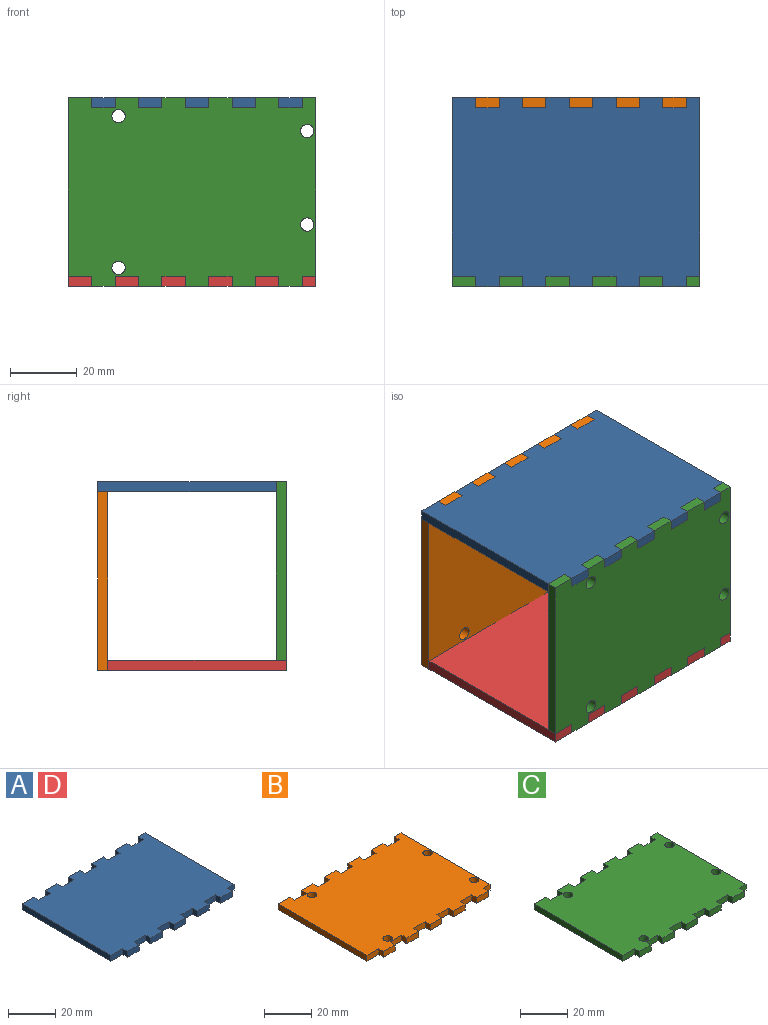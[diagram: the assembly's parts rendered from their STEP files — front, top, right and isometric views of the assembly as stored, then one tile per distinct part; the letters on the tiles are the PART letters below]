
ASSEMBLY  parts=4 mates=3
PART A: 46 faces, bbox 74x56.5x3 mm
  f0: plane 53.5x3mm, normal (-1,0,0), area 160.5mm2, adj f1,f43,f44,f45
  f1: plane 7x3mm, normal (0,-1,0), area 21mm2, adj f0,f2,f44,f45
  f2: plane 3x3mm, normal (-1,0,0), area 9mm2, adj f1,f3,f44,f45
  f3: plane 7x3mm, normal (0,-1,0), area 21mm2, adj f2,f4,f44,f45
  f4: plane 3x3mm, normal (1,0,0), area 9mm2, adj f3,f5,f44,f45
  f5: plane 7x3mm, normal (0,-1,0), area 21mm2, adj f4,f6,f44,f45
  f6: plane 3x3mm, normal (-1,0,0), area 9mm2, adj f5,f7,f44,f45
  f7: plane 7x3mm, normal (0,-1,0), area 21mm2, adj f6,f8,f44,f45
  f8: plane 3x3mm, normal (1,0,0), area 9mm2, adj f7,f9,f44,f45
  f9: plane 7x3mm, normal (0,-1,0), area 21mm2, adj f8,f10,f44,f45
  f10: plane 3x3mm, normal (-1,0,0), area 9mm2, adj f9,f11,f44,f45
  f11: plane 7x3mm, normal (0,-1,0), area 21mm2, adj f10,f12,f44,f45
  f12: plane 3x3mm, normal (1,0,0), area 9mm2, adj f11,f13,f44,f45
  f13: plane 7x3mm, normal (0,-1,0), area 21mm2, adj f12,f14,f44,f45
  f14: plane 3x3mm, normal (-1,0,0), area 9mm2, adj f13,f15,f44,f45
  f15: plane 7x3mm, normal (0,-1,0), area 21mm2, adj f14,f16,f44,f45
  f16: plane 3x3mm, normal (1,0,0), area 9mm2, adj f15,f17,f44,f45
  f17: plane 7x3mm, normal (0,-1,0), area 21mm2, adj f16,f18,f44,f45
  f18: plane 3x3mm, normal (-1,0,0), area 9mm2, adj f17,f19,f44,f45
  f19: plane 7x3mm, normal (0,-1,0), area 21mm2, adj f18,f20,f44,f45
  f20: plane 3x3mm, normal (1,0,0), area 9mm2, adj f19,f21,f44,f45
  f21: plane 4x3mm, normal (0,-1,0), area 12mm2, adj f20,f22,f44,f45
  f22: plane 53.5x3mm, normal (1,0,0), area 160.5mm2, adj f21,f23,f44,f45
  f23: plane 4x3mm, normal (0,1,0), area 12mm2, adj f22,f24,f44,f45
  f24: plane 3x3mm, normal (-1,0,0), area 9mm2, adj f23,f25,f44,f45
  f25: plane 7x3mm, normal (0,1,0), area 21mm2, adj f24,f26,f44,f45
  f26: plane 3x3mm, normal (1,0,0), area 9mm2, adj f25,f27,f44,f45
  f27: plane 7x3mm, normal (0,1,0), area 21mm2, adj f26,f28,f44,f45
  f28: plane 3x3mm, normal (-1,0,0), area 9mm2, adj f27,f29,f44,f45
  f29: plane 7x3mm, normal (0,1,0), area 21mm2, adj f28,f30,f44,f45
  f30: plane 3x3mm, normal (1,0,0), area 9mm2, adj f29,f31,f44,f45
  f31: plane 7x3mm, normal (0,1,0), area 21mm2, adj f30,f32,f44,f45
  f32: plane 3x3mm, normal (-1,0,0), area 9mm2, adj f31,f33,f44,f45
  f33: plane 7x3mm, normal (0,1,0), area 21mm2, adj f32,f34,f44,f45
  f34: plane 3x3mm, normal (1,0,0), area 9mm2, adj f33,f35,f44,f45
  f35: plane 7x3mm, normal (0,1,0), area 21mm2, adj f34,f36,f44,f45
  f36: plane 3x3mm, normal (-1,0,0), area 9mm2, adj f35,f37,f44,f45
  f37: plane 7x3mm, normal (0,1,0), area 21mm2, adj f36,f38,f44,f45
  f38: plane 3x3mm, normal (1,0,0), area 9mm2, adj f37,f39,f44,f45
  f39: plane 7x3mm, normal (0,1,0), area 21mm2, adj f38,f40,f44,f45
  f40: plane 3x3mm, normal (-1,0,0), area 9mm2, adj f39,f41,f44,f45
  f41: plane 7x3mm, normal (0,1,0), area 21mm2, adj f40,f42,f44,f45
  f42: plane 3x3mm, normal (1,0,0), area 9mm2, adj f41,f43,f44,f45
  f43: plane 7x3mm, normal (0,1,0), area 21mm2, adj f0,f42,f44,f45
  f44: plane 74x56.5mm, normal (0,0,1), area 3959mm2, adj f0,f1,f2,f3,f4,f5,f6,f7
  f45: plane 74x56.5mm, normal (0,0,-1), area 3959mm2, adj f0,f1,f2,f3,f4,f5,f6,f7
PART B: 50 faces, bbox 74x56.5x3 mm
  f0: plane 74x56.5mm, normal (0,0,1), area 3908.7mm2, adj f2,f3,f4,f5,f6,f7,f8,f9
  f1: plane 74x56.5mm, normal (0,0,-1), area 3908.7mm2, adj f2,f3,f4,f5,f6,f7,f8,f9
  f2: plane 53.5x3mm, normal (-1,0,0), area 160.5mm2, adj f0,f1,f3,f45
  f3: plane 7x3mm, normal (0,-1,0), area 21mm2, adj f0,f1,f2,f4
  f4: plane 3x3mm, normal (-1,0,0), area 9mm2, adj f0,f1,f3,f5
  f5: plane 7x3mm, normal (0,-1,0), area 21mm2, adj f0,f1,f4,f6
  f6: plane 3x3mm, normal (1,0,0), area 9mm2, adj f0,f1,f5,f7
  f7: plane 7x3mm, normal (0,-1,0), area 21mm2, adj f0,f1,f6,f8
  f8: plane 3x3mm, normal (-1,0,0), area 9mm2, adj f0,f1,f7,f9
  f9: plane 7x3mm, normal (0,-1,0), area 21mm2, adj f0,f1,f8,f10
  f10: plane 3x3mm, normal (1,0,0), area 9mm2, adj f0,f1,f9,f11
  f11: plane 7x3mm, normal (0,-1,0), area 21mm2, adj f0,f1,f10,f12
  f12: plane 3x3mm, normal (-1,0,0), area 9mm2, adj f0,f1,f11,f13
  f13: plane 7x3mm, normal (0,-1,0), area 21mm2, adj f0,f1,f12,f14
  f14: plane 3x3mm, normal (1,0,0), area 9mm2, adj f0,f1,f13,f15
  f15: plane 7x3mm, normal (0,-1,0), area 21mm2, adj f0,f1,f14,f16
  f16: plane 3x3mm, normal (-1,0,0), area 9mm2, adj f0,f1,f15,f17
  f17: plane 7x3mm, normal (0,-1,0), area 21mm2, adj f0,f1,f16,f18
  f18: plane 3x3mm, normal (1,0,0), area 9mm2, adj f0,f1,f17,f19
  f19: plane 7x3mm, normal (0,-1,0), area 21mm2, adj f0,f1,f18,f20
  f20: plane 3x3mm, normal (-1,0,0), area 9mm2, adj f0,f1,f19,f21
  f21: plane 7x3mm, normal (0,-1,0), area 21mm2, adj f0,f1,f20,f22
  f22: plane 3x3mm, normal (1,0,0), area 9mm2, adj f0,f1,f21,f23
  f23: plane 4x3mm, normal (0,-1,0), area 12mm2, adj f0,f1,f22,f24
  f24: plane 53.5x3mm, normal (1,0,0), area 160.5mm2, adj f0,f1,f23,f25
  f25: plane 4x3mm, normal (0,1,0), area 12mm2, adj f0,f1,f24,f26
  f26: plane 3x3mm, normal (-1,0,0), area 9mm2, adj f0,f1,f25,f27
  f27: plane 7x3mm, normal (0,1,0), area 21mm2, adj f0,f1,f26,f28
  f28: plane 3x3mm, normal (1,0,0), area 9mm2, adj f0,f1,f27,f29
  f29: plane 7x3mm, normal (0,1,0), area 21mm2, adj f0,f1,f28,f30
  f30: plane 3x3mm, normal (-1,0,0), area 9mm2, adj f0,f1,f29,f31
  f31: plane 7x3mm, normal (0,1,0), area 21mm2, adj f0,f1,f30,f32
  f32: plane 3x3mm, normal (1,0,0), area 9mm2, adj f0,f1,f31,f33
  f33: plane 7x3mm, normal (0,1,0), area 21mm2, adj f0,f1,f32,f34
  f34: plane 3x3mm, normal (-1,0,0), area 9mm2, adj f0,f1,f33,f35
  f35: plane 7x3mm, normal (0,1,0), area 21mm2, adj f0,f1,f34,f36
  f36: plane 3x3mm, normal (1,0,0), area 9mm2, adj f0,f1,f35,f37
  f37: plane 7x3mm, normal (0,1,0), area 21mm2, adj f0,f1,f36,f38
  f38: plane 3x3mm, normal (-1,0,0), area 9mm2, adj f0,f1,f37,f39
  f39: plane 7x3mm, normal (0,1,0), area 21mm2, adj f0,f1,f38,f40
  f40: plane 3x3mm, normal (1,0,0), area 9mm2, adj f0,f1,f39,f41
  f41: plane 7x3mm, normal (0,1,0), area 21mm2, adj f0,f1,f40,f42
  f42: plane 3x3mm, normal (-1,0,0), area 9mm2, adj f0,f1,f41,f43
  f43: plane 7x3mm, normal (0,1,0), area 21mm2, adj f0,f1,f42,f44
  f44: plane 3x3mm, normal (1,0,0), area 9mm2, adj f0,f1,f43,f45
  f45: plane 7x3mm, normal (0,1,0), area 21mm2, adj f0,f1,f2,f44
  f46: cylinder r=2mm len=4mm, axis (0,0,1), area 37.7mm2, adj f0,f1
  f47: cylinder r=2mm len=4mm, axis (0,0,1), area 37.7mm2, adj f0,f1
  f48: cylinder r=2mm len=4mm, axis (0,0,1), area 37.7mm2, adj f0,f1
  f49: cylinder r=2mm len=4mm, axis (0,0,1), area 37.7mm2, adj f0,f1
PART C: 50 faces, bbox 74x56.5x3 mm
  f0: plane 74x56.5mm, normal (0,0,1), area 3908.7mm2, adj f2,f3,f4,f5,f6,f7,f8,f9
  f1: plane 74x56.5mm, normal (0,0,-1), area 3908.7mm2, adj f2,f3,f4,f5,f6,f7,f8,f9
  f2: plane 53.5x3mm, normal (-1,0,0), area 160.5mm2, adj f0,f1,f3,f45
  f3: plane 7x3mm, normal (0,-1,0), area 21mm2, adj f0,f1,f2,f4
  f4: plane 3x3mm, normal (-1,0,0), area 9mm2, adj f0,f1,f3,f5
  f5: plane 7x3mm, normal (0,-1,0), area 21mm2, adj f0,f1,f4,f6
  f6: plane 3x3mm, normal (1,0,0), area 9mm2, adj f0,f1,f5,f7
  f7: plane 7x3mm, normal (0,-1,0), area 21mm2, adj f0,f1,f6,f8
  f8: plane 3x3mm, normal (-1,0,0), area 9mm2, adj f0,f1,f7,f9
  f9: plane 7x3mm, normal (0,-1,0), area 21mm2, adj f0,f1,f8,f10
  f10: plane 3x3mm, normal (1,0,0), area 9mm2, adj f0,f1,f9,f11
  f11: plane 7x3mm, normal (0,-1,0), area 21mm2, adj f0,f1,f10,f12
  f12: plane 3x3mm, normal (-1,0,0), area 9mm2, adj f0,f1,f11,f13
  f13: plane 7x3mm, normal (0,-1,0), area 21mm2, adj f0,f1,f12,f14
  f14: plane 3x3mm, normal (1,0,0), area 9mm2, adj f0,f1,f13,f15
  f15: plane 7x3mm, normal (0,-1,0), area 21mm2, adj f0,f1,f14,f16
  f16: plane 3x3mm, normal (-1,0,0), area 9mm2, adj f0,f1,f15,f17
  f17: plane 7x3mm, normal (0,-1,0), area 21mm2, adj f0,f1,f16,f18
  f18: plane 3x3mm, normal (1,0,0), area 9mm2, adj f0,f1,f17,f19
  f19: plane 7x3mm, normal (0,-1,0), area 21mm2, adj f0,f1,f18,f20
  f20: plane 3x3mm, normal (-1,0,0), area 9mm2, adj f0,f1,f19,f21
  f21: plane 7x3mm, normal (0,-1,0), area 21mm2, adj f0,f1,f20,f22
  f22: plane 3x3mm, normal (1,0,0), area 9mm2, adj f0,f1,f21,f23
  f23: plane 4x3mm, normal (0,-1,0), area 12mm2, adj f0,f1,f22,f24
  f24: plane 53.5x3mm, normal (1,0,0), area 160.5mm2, adj f0,f1,f23,f25
  f25: plane 4x3mm, normal (0,1,0), area 12mm2, adj f0,f1,f24,f26
  f26: plane 3x3mm, normal (-1,0,0), area 9mm2, adj f0,f1,f25,f27
  f27: plane 7x3mm, normal (0,1,0), area 21mm2, adj f0,f1,f26,f28
  f28: plane 3x3mm, normal (1,0,0), area 9mm2, adj f0,f1,f27,f29
  f29: plane 7x3mm, normal (0,1,0), area 21mm2, adj f0,f1,f28,f30
  f30: plane 3x3mm, normal (-1,0,0), area 9mm2, adj f0,f1,f29,f31
  f31: plane 7x3mm, normal (0,1,0), area 21mm2, adj f0,f1,f30,f32
  f32: plane 3x3mm, normal (1,0,0), area 9mm2, adj f0,f1,f31,f33
  f33: plane 7x3mm, normal (0,1,0), area 21mm2, adj f0,f1,f32,f34
  f34: plane 3x3mm, normal (-1,0,0), area 9mm2, adj f0,f1,f33,f35
  f35: plane 7x3mm, normal (0,1,0), area 21mm2, adj f0,f1,f34,f36
  f36: plane 3x3mm, normal (1,0,0), area 9mm2, adj f0,f1,f35,f37
  f37: plane 7x3mm, normal (0,1,0), area 21mm2, adj f0,f1,f36,f38
  f38: plane 3x3mm, normal (-1,0,0), area 9mm2, adj f0,f1,f37,f39
  f39: plane 7x3mm, normal (0,1,0), area 21mm2, adj f0,f1,f38,f40
  f40: plane 3x3mm, normal (1,0,0), area 9mm2, adj f0,f1,f39,f41
  f41: plane 7x3mm, normal (0,1,0), area 21mm2, adj f0,f1,f40,f42
  f42: plane 3x3mm, normal (-1,0,0), area 9mm2, adj f0,f1,f41,f43
  f43: plane 7x3mm, normal (0,1,0), area 21mm2, adj f0,f1,f42,f44
  f44: plane 3x3mm, normal (1,0,0), area 9mm2, adj f0,f1,f43,f45
  f45: plane 7x3mm, normal (0,1,0), area 21mm2, adj f0,f1,f2,f44
  f46: cylinder r=2mm len=4mm, axis (0,0,-1), area 37.7mm2, adj f0,f1
  f47: cylinder r=2mm len=4mm, axis (0,0,-1), area 37.7mm2, adj f0,f1
  f48: cylinder r=2mm len=4mm, axis (0,0,-1), area 37.7mm2, adj f0,f1
  f49: cylinder r=2mm len=4mm, axis (0,0,-1), area 37.7mm2, adj f0,f1
PART D: same geometry as A
PLACE A t=(-14.97,8.04,23.52)mm
PLACE B rot(axis=(-1,0,0),90deg) t=(-14.97,-105.31,-1.73)mm
PLACE C rot(axis=(1,0,0),90deg) t=(-14.97,-79.91,-1.73)mm
PLACE D rot(axis=(1,0,0),180deg) t=(-14.97,8.04,-26.98)mm
MATE parallel D.f20 <-> B.f26  axis (1,0,0) through (18.03,34.79,-28.48)mm
MATE parallel B.f22 <-> A.f24  axis (1,0,0) through (18.03,34.79,25.02)mm
MATE parallel C.f4 <-> D.f42  axis (-1,0,0) through (-44.97,-18.71,-28.48)mm
